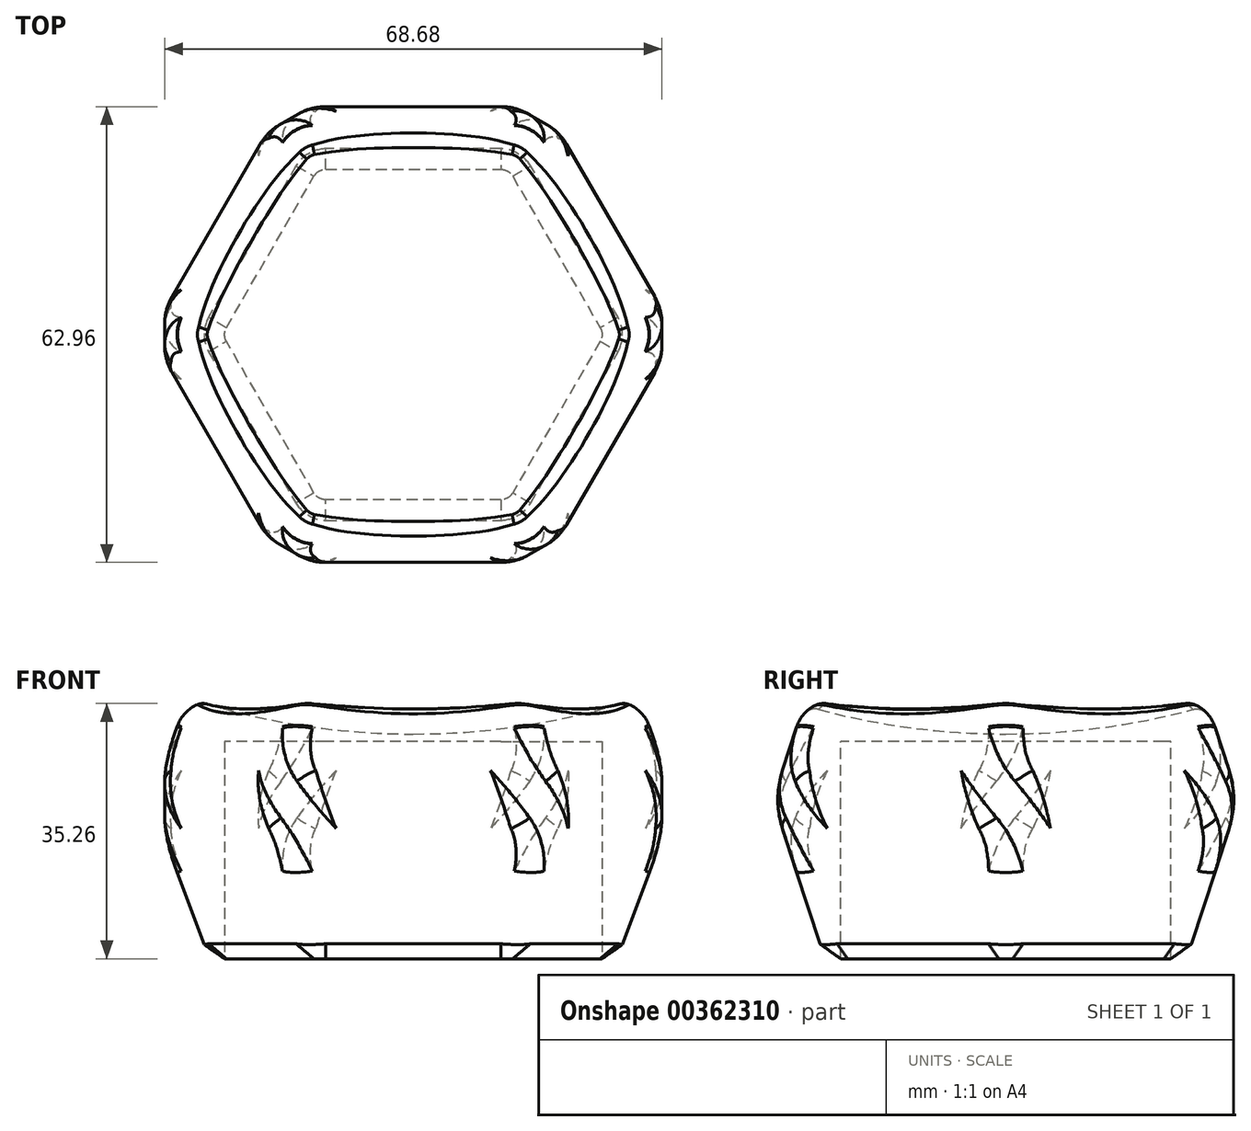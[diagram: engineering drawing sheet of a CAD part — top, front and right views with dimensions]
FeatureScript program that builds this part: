
annotation { "Feature Type Name" : "Feature", "Feature Type Description" : "" }
export const myFeature = defineFeature(function(context is Context, id is Id, definition is map)
    precondition{}
    {
        {
            var Q0;
            Q0=qCreatedBy(makeId("Top.planeOp"),FACE);
            var sketch = newSketch(context, id + "F0", { "sketchPlane" : qUnion([Q0])});
            skCircle(sketch, "E0.cCircle", {"center": v(0, 0) * mm, "radius": 28.87 * mm, "construction": true});
            skLineSegment(sketch, "E0.0", {"start": v(14.43, 25) * mm, "end": v(28.87, 0) * mm});
            skLineSegment(sketch, "E0.1", {"start": v(28.87, 0) * mm, "end": v(14.43, -25) * mm});
            skLineSegment(sketch, "E0.2", {"start": v(14.43, -25) * mm, "end": v(-14.43, -25) * mm});
            skLineSegment(sketch, "E0.3", {"start": v(-14.43, -25) * mm, "end": v(-28.87, 0) * mm});
            skLineSegment(sketch, "E0.4", {"start": v(-28.87, 0) * mm, "end": v(-14.43, 25) * mm});
            skLineSegment(sketch, "E0.5", {"start": v(-14.43, 25) * mm, "end": v(14.43, 25) * mm});
            skSolve(sketch);
        }
        {
            var Q0;
            Q0 = qSketchRegion(id + "F0", true);
            extrude(context, id + "F1", {"entities" : qUnion([Q0]), "depth" : 22 * mm, "hasDraft" : true, "draftAngle" : 18 * degree});
        }
        {
            var Q0;
            Q0=makeQuery(id+"F1.opExtrude","CAP_FACE",FACE,{"disambiguationData":[OSD([sQuery(id+"F0.wireOp",EDGE,"E0.0"),sQuery(id+"F0.wireOp",EDGE,"E0.1"),sQuery(id+"F0.wireOp",EDGE,"E0.2"),sQuery(id+"F0.wireOp",EDGE,"E0.3"),sQuery(id+"F0.wireOp",EDGE,"E0.4"),sQuery(id+"F0.wireOp",EDGE,"E0.5")])],"isStart":false});
            extrude(context, id + "F2", {"entities" : qUnion([Q0]), "operationType" : NewBodyOperationType.ADD, "depth" : 13.5 * mm, "hasDraft" : true, "draftAngle" : 18 * degree, "draftPullDirection" : true});
        }
        {
            var Q0;
            Q0=makeQuery(id+"F2.opExtrude","CAP_FACE",FACE,{"disambiguationData":[OSD([sQuery(id+"F0.wireOp",EDGE,"E0.0"),sQuery(id+"F0.wireOp",EDGE,"E0.1"),sQuery(id+"F0.wireOp",EDGE,"E0.2"),sQuery(id+"F0.wireOp",EDGE,"E0.3"),sQuery(id+"F0.wireOp",EDGE,"E0.4"),sQuery(id+"F0.wireOp",EDGE,"E0.5")])],"isStart":false});
            var Q1;
            Q1=makeQuery(id+"F2.opExtrude","SWEPT_EDGE",EDGE,{"disambiguationData":[OSD([sQuery(id+"F0.wireOp",EDGE,"E0.3"),sQuery(id+"F0.wireOp",EDGE,"E0.4")])]});
            var Q2;
            Q2=makeQuery(id+"F2.opExtrude","SWEPT_EDGE",EDGE,{"disambiguationData":[OSD([sQuery(id+"F0.wireOp",EDGE,"E0.2"),sQuery(id+"F0.wireOp",EDGE,"E0.3")])]});
            var Q3;
            Q3=makeQuery(id+"F2.opExtrude","SWEPT_EDGE",EDGE,{"disambiguationData":[OSD([sQuery(id+"F0.wireOp",EDGE,"E0.1"),sQuery(id+"F0.wireOp",EDGE,"E0.2")])]});
            var Q4;
            Q4=makeQuery(id+"F2.opExtrude","SWEPT_EDGE",EDGE,{"disambiguationData":[OSD([sQuery(id+"F0.wireOp",EDGE,"E0.4"),sQuery(id+"F0.wireOp",EDGE,"E0.5")])]});
            var Q5;
            Q5=makeQuery(id+"F2.opExtrude","SWEPT_EDGE",EDGE,{"disambiguationData":[OSD([sQuery(id+"F0.wireOp",EDGE,"E0.0"),sQuery(id+"F0.wireOp",EDGE,"E0.5")])]});
            var Q6;
            Q6=makeQuery(id+"F2.opExtrude","SWEPT_EDGE",EDGE,{"disambiguationData":[OSD([sQuery(id+"F0.wireOp",EDGE,"E0.0"),sQuery(id+"F0.wireOp",EDGE,"E0.1")])]});
            var Q7;
            Q7=makeQuery(id+"F1.opExtrude","SWEPT_EDGE",EDGE,{"disambiguationData":[OSD([sQuery(id+"F0.wireOp",EDGE,"E0.0"),sQuery(id+"F0.wireOp",EDGE,"E0.1")])]});
            var Q8;
            Q8=makeQuery(id+"F1.opExtrude","SWEPT_EDGE",EDGE,{"disambiguationData":[OSD([sQuery(id+"F0.wireOp",EDGE,"E0.0"),sQuery(id+"F0.wireOp",EDGE,"E0.5")])]});
            var Q9;
            Q9=makeQuery(id+"F1.opExtrude","SWEPT_EDGE",EDGE,{"disambiguationData":[OSD([sQuery(id+"F0.wireOp",EDGE,"E0.4"),sQuery(id+"F0.wireOp",EDGE,"E0.5")])]});
            var Q10;
            Q10=makeQuery(id+"F1.opExtrude","SWEPT_EDGE",EDGE,{"disambiguationData":[OSD([sQuery(id+"F0.wireOp",EDGE,"E0.1"),sQuery(id+"F0.wireOp",EDGE,"E0.2")])]});
            var Q11;
            Q11=makeQuery(id+"F1.opExtrude","SWEPT_EDGE",EDGE,{"disambiguationData":[OSD([sQuery(id+"F0.wireOp",EDGE,"E0.2"),sQuery(id+"F0.wireOp",EDGE,"E0.3")])]});
            var Q12;
            Q12=makeQuery(id+"F1.opExtrude","SWEPT_EDGE",EDGE,{"disambiguationData":[OSD([sQuery(id+"F0.wireOp",EDGE,"E0.3"),sQuery(id+"F0.wireOp",EDGE,"E0.4")])]});
            fillet(context, id + "F3", {"entities" : qUnion([Q0, Q1, Q2, Q3, Q4, Q5, Q6, Q7, Q8, Q9, Q10, Q11, Q12]), "radius" : 5 * mm, "tangentPropagation" : true, "allowEdgeOverflow" : false});
        }
        {
            var Q0;
            Q0=makeQuery(id+"F1.opExtrude","CAP_FACE",FACE,{"disambiguationData":[OSD([sQuery(id+"F0.wireOp",EDGE,"E0.0"),sQuery(id+"F0.wireOp",EDGE,"E0.1"),sQuery(id+"F0.wireOp",EDGE,"E0.2"),sQuery(id+"F0.wireOp",EDGE,"E0.3"),sQuery(id+"F0.wireOp",EDGE,"E0.4"),sQuery(id+"F0.wireOp",EDGE,"E0.5")])],"isStart":true});
            chamfer(context, id + "F4", {"entities" : qUnion([Q0]), "width" : 3 * mm, "tangentPropagation" : true});
        }
        {
            var Q0;
            {var subQ0=sQuery(id+"F0.wireOp",EDGE,"E0.4");Q0=makeQuery(id+"F2.boolean.opBoolean","MERGE",EDGE,{"derivedFrom":[makeQuery(id+"F1.opExtrude","CAP_EDGE",EDGE,{"disambiguationData":[OSD([subQ0])],"isStart":false}),makeQuery(id+"F2.opExtrude","CAP_EDGE",EDGE,{"disambiguationData":[OSD([subQ0])],"isStart":true})]});}
            fillet(context, id + "F5", {"entities" : qUnion([Q0]), "radius" : 13 * mm, "tangentPropagation" : true, "allowEdgeOverflow" : false});
        }
        {
            var Q0;
            Q0=qCreatedBy(makeId("Front.planeOp"),FACE);
            var sketch = newSketch(context, id + "F6", { "sketchPlane" : qUnion([Q0])});
            skArc(sketch, "E1", {"start": v(0, 31.05) * mm, "mid": v(100, 131.05) * mm, "end": v(0, 231.05) * mm});
            skLineSegment(sketch, "E2", {"start": v(0, 231.05) * mm, "end": v(0, 31.05) * mm});
            skSolve(sketch);
        }
        {
            var Q0;
            Q0 = qSketchRegion(id + "F6", true);
            var Q1;
            Q1=sQuery(id+"F6.wireOp",EDGE,"E2");
            revolve(context, id + "F7", {"operationType" : NewBodyOperationType.REMOVE, "entities" : qUnion([Q0]), "axis" : qUnion([Q1]), "revolveType" : RevolveType.FULL, "oppositeDirection" : true});
        }
        {
            var Q0;
            Q0=makeQuery(id+"F7.boolean.opBoolean","INTERSECT",EDGE,{"derivedFrom":[makeQuery(id+"F3.opFillet","BLEND_FACE",FACE,{"disambiguationData":[OSD([sQuery(id+"F0.wireOp",EDGE,"E0.3")])]}),makeQuery(id+"F7.opRevolve","SWEPT_FACE",FACE,{"disambiguationData":[OSD([sQuery(id+"F6.wireOp",EDGE,"E1")])]})]});
            fillet(context, id + "F8", {"entities" : qUnion([Q0]), "radius" : 2 * mm, "tangentPropagation" : true, "allowEdgeOverflow" : false});
        }
        {
            var Q0;
            Q0=makeQuery(id+"F1.opExtrude","CAP_FACE",FACE,{"disambiguationData":[OSD([sQuery(id+"F0.wireOp",EDGE,"E0.0"),sQuery(id+"F0.wireOp",EDGE,"E0.1"),sQuery(id+"F0.wireOp",EDGE,"E0.2"),sQuery(id+"F0.wireOp",EDGE,"E0.3"),sQuery(id+"F0.wireOp",EDGE,"E0.4"),sQuery(id+"F0.wireOp",EDGE,"E0.5")])],"isStart":true});
            extrude(context, id + "F9", {"entities" : qUnion([Q0]), "operationType" : NewBodyOperationType.REMOVE, "oppositeDirection" : true, "depth" : 30 * mm});
        }
    });
